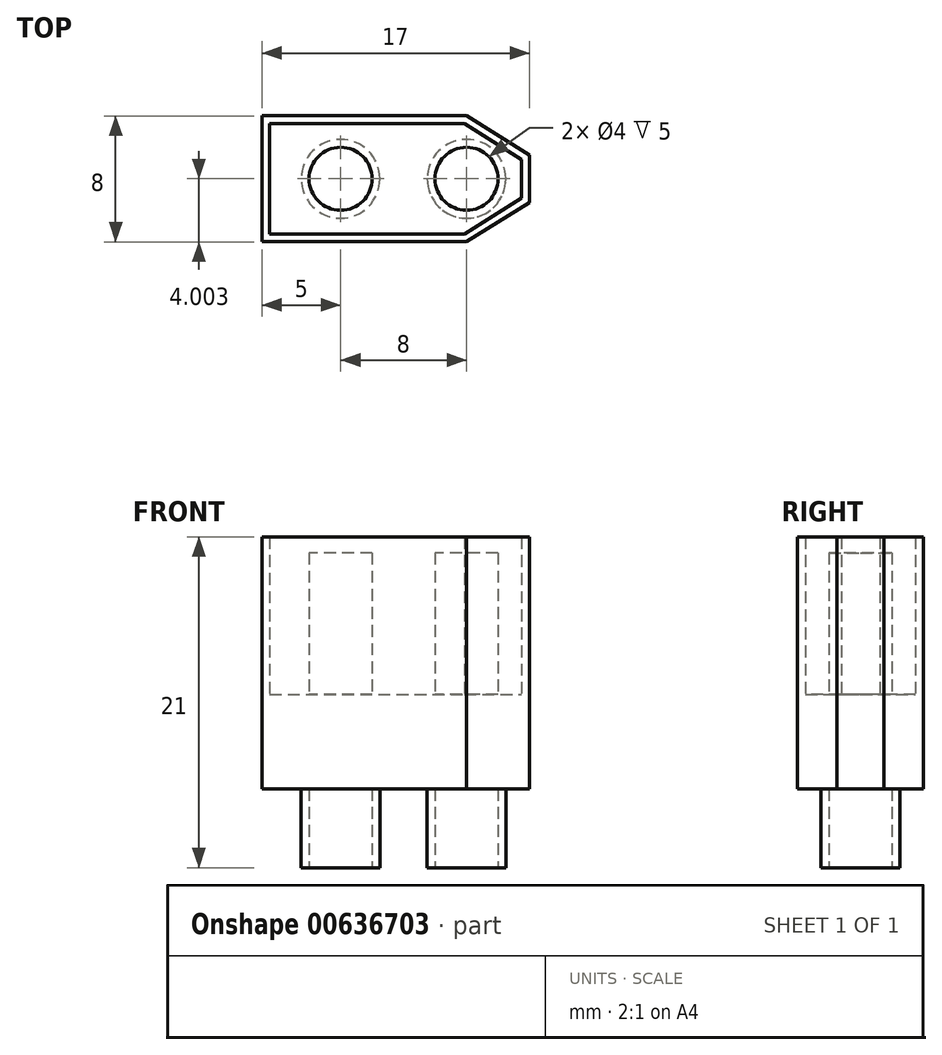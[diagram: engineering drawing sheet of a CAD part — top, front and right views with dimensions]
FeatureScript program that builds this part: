
annotation { "Feature Type Name" : "Feature", "Feature Type Description" : "" }
export const myFeature = defineFeature(function(context is Context, id is Id, definition is map)
    precondition{}
    {
        {
            var Q0;
            Q0=qCreatedBy(makeId("Top.planeOp"),FACE);
            var sketch = newSketch(context, id + "F0", { "sketchPlane" : qUnion([Q0])});
            skLineSegment(sketch, "E0.bottom", {"start": v(-13, -7.17) * mm, "end": v(0, -7.17) * mm});
            skLineSegment(sketch, "E0.top", {"start": v(-13, 0.83) * mm, "end": v(0, 0.83) * mm});
            skLineSegment(sketch, "E0.left", {"start": v(-13, -7.17) * mm, "end": v(-13, 0.83) * mm});
            skLineSegment(sketch, "E1", {"start": v(0, 0.83) * mm, "end": v(4, -1.67) * mm});
            skLineSegment(sketch, "E2", {"start": v(4, -1.67) * mm, "end": v(4, -4.67) * mm});
            skLineSegment(sketch, "E3", {"start": v(4, -4.67) * mm, "end": v(0, -7.17) * mm});
            skSolve(sketch);
        }
        {
            var Q0;
            Q0=makeQuery(id+"F0.imprint","IMPRINT",FACE,{"disambiguationData":[TD([[makeQuery(id+"F0.imprint","IMPRINT",EDGE,{"derivedFrom":sQuery(id+"F0.wireOp",EDGE,"E0.bottom")}),1.0]])]});
            extrude(context, id + "F1", {"entities" : qUnion([Q0]), "depth" : 6 * mm, "offsetDistance" : 25 * mm});
        }
        {
            var Q0;
            Q0=makeQuery(id+"F1.opExtrude","CAP_FACE",FACE,{"disambiguationData":[OSD([sQuery(id+"F0.wireOp",EDGE,"E0.bottom"),sQuery(id+"F0.wireOp",EDGE,"E0.top"),sQuery(id+"F0.wireOp",EDGE,"E0.left"),sQuery(id+"F0.wireOp",EDGE,"E1"),sQuery(id+"F0.wireOp",EDGE,"E2"),sQuery(id+"F0.wireOp",EDGE,"E3")])],"isStart":false});
            var sketch = newSketch(context, id + "F2", { "sketchPlane" : qUnion([Q0])});
            skLineSegment(sketch, "E4.0", {"start": v(-10.61, -7.67) * mm, "end": v(2.39, -7.67) * mm});
            skLineSegment(sketch, "E5.0", {"start": v(-0.14, 0.33) * mm, "end": v(3.5, -1.94) * mm});
            skLineSegment(sketch, "E5.1", {"start": v(3.5, -4.4) * mm, "end": v(-0.14, -6.67) * mm});
            skLineSegment(sketch, "E5.2", {"start": v(-12.5, -6.67) * mm, "end": v(-0.14, -6.67) * mm});
            skLineSegment(sketch, "E5.3", {"start": v(3.5, -1.94) * mm, "end": v(3.5, -4.4) * mm});
            skLineSegment(sketch, "E5.4", {"start": v(-12.5, -6.67) * mm, "end": v(-12.5, 0.33) * mm});
            skLineSegment(sketch, "E5.5", {"start": v(-12.5, 0.33) * mm, "end": v(-0.14, 0.33) * mm});
            skSolve(sketch);
        }
        {
            var Q0;
            Q0=makeQuery(id+"F2.imprint","IMPRINT",FACE,{"disambiguationData":[TD([[makeQuery(id+"F2.imprint","IMPRINT",EDGE,{"derivedFrom":sQuery(id+"F2.wireOp",EDGE,"E5.0")}),1.0]])]});
            extrude(context, id + "F3", {"entities" : qUnion([Q0]), "operationType" : NewBodyOperationType.ADD, "depth" : 10 * mm, "offsetDistance" : 25 * mm});
        }
        {
            var Q0;
            Q0=makeQuery(id+"F1.opExtrude","CAP_FACE",FACE,{"disambiguationData":[OSD([sQuery(id+"F0.wireOp",EDGE,"E0.bottom"),sQuery(id+"F0.wireOp",EDGE,"E0.top"),sQuery(id+"F0.wireOp",EDGE,"E0.left"),sQuery(id+"F0.wireOp",EDGE,"E1"),sQuery(id+"F0.wireOp",EDGE,"E2"),sQuery(id+"F0.wireOp",EDGE,"E3")])],"isStart":true});
            var sketch = newSketch(context, id + "F4", { "sketchPlane" : qUnion([Q0])});
            skCircle(sketch, "E6", {"center": v(-8, 3.17) * mm, "radius": 2.5 * mm});
            skCircle(sketch, "E7", {"center": v(0, 3.17) * mm, "radius": 2.5 * mm});
            skSolve(sketch);
        }
        {
            var Q0;
            Q0=makeQuery(id+"F4.imprint","IMPRINT",FACE,{"disambiguationData":[TD([[makeQuery(id+"F4.imprint","IMPRINT",EDGE,{"derivedFrom":sQuery(id+"F4.wireOp",EDGE,"E7")}),1.0]])]});
            var Q1;
            Q1=makeQuery(id+"F4.imprint","IMPRINT",FACE,{"disambiguationData":[TD([[makeQuery(id+"F4.imprint","IMPRINT",EDGE,{"derivedFrom":sQuery(id+"F4.wireOp",EDGE,"E6")}),1.0]])]});
            extrude(context, id + "F5", {"entities" : qUnion([Q0, Q1]), "operationType" : NewBodyOperationType.ADD, "depth" : 5 * mm, "offsetDistance" : 25 * mm, "hasDraft" : true, "draftAngle" : 0 * degree});
        }
        {
            var Q0;
            Q0=makeQuery(id+"F5.opExtrude","CAP_FACE",FACE,{"disambiguationData":[OSD([sQuery(id+"F4.wireOp",EDGE,"E6")])],"isStart":false});
            var sketch = newSketch(context, id + "F6", { "sketchPlane" : qUnion([Q0])});
            skCircle(sketch, "E8.0", {"center": v(-8, 3.17) * mm, "radius": 2 * mm});
            skCircle(sketch, "E9.0", {"center": v(0, 3.17) * mm, "radius": 2 * mm});
            skSolve(sketch);
        }
        {
            var Q0;
            Q0=makeQuery(id+"F6.imprint","IMPRINT",FACE,{"disambiguationData":[TD([[makeQuery(id+"F6.imprint","IMPRINT",EDGE,{"derivedFrom":sQuery(id+"F6.wireOp",EDGE,"E8.0")}),1.0]])]});
            var Q1;
            Q1=makeQuery(id+"F6.imprint","IMPRINT",FACE,{"disambiguationData":[TD([[makeQuery(id+"F6.imprint","IMPRINT",EDGE,{"derivedFrom":sQuery(id+"F6.wireOp",EDGE,"E9.0")}),1.0]])]});
            extrude(context, id + "F7", {"entities" : qUnion([Q0, Q1]), "operationType" : NewBodyOperationType.REMOVE, "oppositeDirection" : true, "depth" : 5 * mm, "offsetDistance" : 25 * mm});
        }
        {
            var Q0;
            Q0=makeQuery(id+"F1.opExtrude","CAP_FACE",FACE,{"disambiguationData":[OSD([sQuery(id+"F0.wireOp",EDGE,"E0.bottom"),sQuery(id+"F0.wireOp",EDGE,"E0.top"),sQuery(id+"F0.wireOp",EDGE,"E0.left"),sQuery(id+"F0.wireOp",EDGE,"E1"),sQuery(id+"F0.wireOp",EDGE,"E2"),sQuery(id+"F0.wireOp",EDGE,"E3")])],"isStart":false});
            var sketch = newSketch(context, id + "F8", { "sketchPlane" : qUnion([Q0])});
            skCircle(sketch, "E10.0", {"center": v(-8, -3.17) * mm, "radius": 2 * mm});
            skCircle(sketch, "E11.0", {"center": v(0, -3.17) * mm, "radius": 2 * mm});
            skSolve(sketch);
        }
        {
            var Q0;
            Q0=makeQuery(id+"F8.imprint","IMPRINT",FACE,{"disambiguationData":[TD([[makeQuery(id+"F8.imprint","IMPRINT",EDGE,{"derivedFrom":sQuery(id+"F8.wireOp",EDGE,"E10.0")}),1.0]])]});
            var Q1;
            Q1=makeQuery(id+"F8.imprint","IMPRINT",FACE,{"disambiguationData":[TD([[makeQuery(id+"F8.imprint","IMPRINT",EDGE,{"derivedFrom":sQuery(id+"F8.wireOp",EDGE,"E11.0")}),1.0]])]});
            extrude(context, id + "F9", {"entities" : qUnion([Q0, Q1]), "operationType" : NewBodyOperationType.ADD, "depth" : 9 * mm, "offsetDistance" : 25 * mm});
        }
    });
